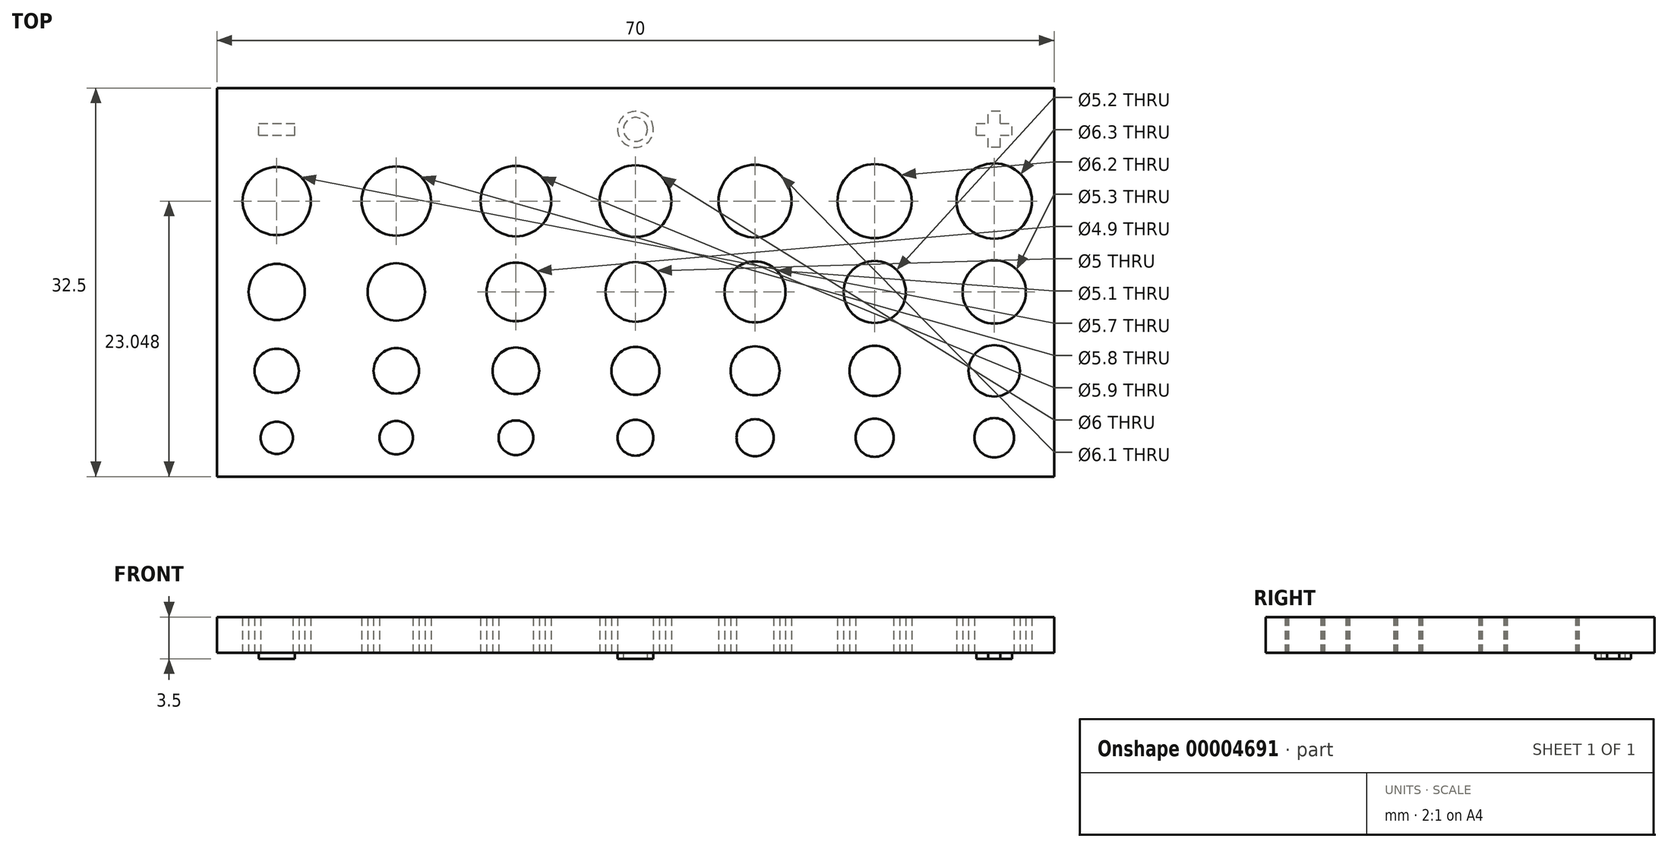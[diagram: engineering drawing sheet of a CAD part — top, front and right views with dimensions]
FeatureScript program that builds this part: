
annotation { "Feature Type Name" : "Feature", "Feature Type Description" : "" }
export const myFeature = defineFeature(function(context is Context, id is Id, definition is map)
    precondition{}
    {
        {
            var Q0;
            Q0=qCreatedBy(makeId("Top.planeOp"),FACE);
            var sketch = newSketch(context, id + "F0", { "sketchPlane" : qUnion([Q0])});
            skLineSegment(sketch, "E0.bottom", {"start": v(0, 0) * mm, "end": v(70, 0) * mm});
            skLineSegment(sketch, "E0.top", {"start": v(0, 32.5) * mm, "end": v(70, 32.5) * mm});
            skLineSegment(sketch, "E0.left", {"start": v(0, 0) * mm, "end": v(0, 32.5) * mm});
            skLineSegment(sketch, "E0.right", {"start": v(70, 0) * mm, "end": v(70, 32.5) * mm});
            skSolve(sketch);
        }
        {
            var Q0;
            Q0=makeQuery(id+"F0.imprint","IMPRINT",FACE,{"disambiguationData":[TD([[makeQuery(id+"F0.imprint","IMPRINT",EDGE,{"derivedFrom":sQuery(id+"F0.wireOp",EDGE,"E0.bottom")}),1.0]])]});
            extrude(context, id + "F1", {"entities" : qUnion([Q0]), "depth" : 3 * mm});
        }
        {
            var Q0;
            Q0=qCreatedBy(makeId("Top.planeOp"),FACE);
            var sketch = newSketch(context, id + "F2", { "sketchPlane" : qUnion([Q0])});
            skLineSegment(sketch, "E1", {"start": v(-5, 15.45) * mm, "end": v(5, 15.45) * mm, "construction": true});
            skLineSegment(sketch, "E2", {"start": v(5, 15.45) * mm, "end": v(15, 15.45) * mm, "construction": true});
            skLineSegment(sketch, "E3", {"start": v(15, 15.45) * mm, "end": v(25, 15.45) * mm, "construction": true});
            skLineSegment(sketch, "E4", {"start": v(25, 15.45) * mm, "end": v(35, 15.45) * mm, "construction": true});
            skLineSegment(sketch, "E5", {"start": v(35, 15.45) * mm, "end": v(45, 15.45) * mm, "construction": true});
            skLineSegment(sketch, "E6", {"start": v(45, 15.45) * mm, "end": v(55, 15.45) * mm, "construction": true});
            skLineSegment(sketch, "E7", {"start": v(-5, 23.05) * mm, "end": v(5, 23.05) * mm, "construction": true});
            skLineSegment(sketch, "E8", {"start": v(5, 23.05) * mm, "end": v(15, 23.05) * mm, "construction": true});
            skLineSegment(sketch, "E9", {"start": v(15, 23.05) * mm, "end": v(25, 23.05) * mm, "construction": true});
            skLineSegment(sketch, "E10", {"start": v(25, 23.05) * mm, "end": v(35, 23.05) * mm, "construction": true});
            skLineSegment(sketch, "E11", {"start": v(35, 23.05) * mm, "end": v(45, 23.05) * mm, "construction": true});
            skLineSegment(sketch, "E12", {"start": v(45, 23.05) * mm, "end": v(55, 23.05) * mm, "construction": true});
            skLineSegment(sketch, "E13", {"start": v(55, 3.25) * mm, "end": v(45, 3.25) * mm, "construction": true});
            skLineSegment(sketch, "E14", {"start": v(45, 3.25) * mm, "end": v(35, 3.25) * mm, "construction": true});
            skLineSegment(sketch, "E15", {"start": v(35, 3.25) * mm, "end": v(25, 3.25) * mm, "construction": true});
            skLineSegment(sketch, "E16", {"start": v(25, 3.25) * mm, "end": v(15, 3.25) * mm, "construction": true});
            skLineSegment(sketch, "E17", {"start": v(15, 3.25) * mm, "end": v(5, 3.25) * mm, "construction": true});
            skLineSegment(sketch, "E18", {"start": v(5, 3.25) * mm, "end": v(-5, 3.25) * mm, "construction": true});
            skCircle(sketch, "E19", {"center": v(5, 15.45) * mm, "radius": 2.35 * mm});
            skCircle(sketch, "E20", {"center": v(15, 15.45) * mm, "radius": 2.4 * mm});
            skCircle(sketch, "E21", {"center": v(25, 15.45) * mm, "radius": 2.45 * mm});
            skCircle(sketch, "E22", {"center": v(35, 15.45) * mm, "radius": 2.5 * mm});
            skCircle(sketch, "E23", {"center": v(45, 15.45) * mm, "radius": 2.55 * mm});
            skCircle(sketch, "E24", {"center": v(5, 23.05) * mm, "radius": 2.85 * mm});
            skCircle(sketch, "E25", {"center": v(15, 23.05) * mm, "radius": 2.9 * mm});
            skCircle(sketch, "E26", {"center": v(25, 23.05) * mm, "radius": 2.95 * mm});
            skCircle(sketch, "E27", {"center": v(35, 23.05) * mm, "radius": 3 * mm});
            skCircle(sketch, "E28", {"center": v(45, 23.05) * mm, "radius": 3.05 * mm});
            skCircle(sketch, "E29", {"center": v(5, 3.25) * mm, "radius": 1.35 * mm});
            skCircle(sketch, "E30", {"center": v(15, 3.25) * mm, "radius": 1.4 * mm});
            skCircle(sketch, "E31", {"center": v(25, 3.25) * mm, "radius": 1.45 * mm});
            skCircle(sketch, "E32", {"center": v(35, 3.25) * mm, "radius": 1.5 * mm});
            skCircle(sketch, "E33", {"center": v(45, 3.25) * mm, "radius": 1.55 * mm});
            skLineSegment(sketch, "E34", {"start": v(-5, 8.85) * mm, "end": v(5, 8.85) * mm, "construction": true});
            skLineSegment(sketch, "E35", {"start": v(5, 8.85) * mm, "end": v(15, 8.85) * mm, "construction": true});
            skLineSegment(sketch, "E36", {"start": v(15, 8.85) * mm, "end": v(25, 8.85) * mm, "construction": true});
            skLineSegment(sketch, "E37", {"start": v(25, 8.85) * mm, "end": v(35, 8.85) * mm, "construction": true});
            skLineSegment(sketch, "E38", {"start": v(35, 8.85) * mm, "end": v(45, 8.85) * mm, "construction": true});
            skLineSegment(sketch, "E39", {"start": v(45, 8.85) * mm, "end": v(55, 8.85) * mm, "construction": true});
            skCircle(sketch, "E40", {"center": v(5, 8.85) * mm, "radius": 1.85 * mm});
            skCircle(sketch, "E41", {"center": v(15, 8.85) * mm, "radius": 1.9 * mm});
            skCircle(sketch, "E42", {"center": v(25, 8.85) * mm, "radius": 1.95 * mm});
            skCircle(sketch, "E43", {"center": v(35, 8.85) * mm, "radius": 2 * mm});
            skCircle(sketch, "E44", {"center": v(45, 8.85) * mm, "radius": 2.05 * mm});
            skLineSegment(sketch, "E45", {"start": v(45, 3.25) * mm, "end": v(45, 8.85) * mm, "construction": true});
            skLineSegment(sketch, "E46", {"start": v(45, 8.85) * mm, "end": v(45, 15.45) * mm, "construction": true});
            skLineSegment(sketch, "E47", {"start": v(45, 23.05) * mm, "end": v(45, 15.45) * mm, "construction": true});
            skLineSegment(sketch, "E48", {"start": v(55, 3.25) * mm, "end": v(65, 3.25) * mm, "construction": true});
            skLineSegment(sketch, "E49", {"start": v(65, 3.25) * mm, "end": v(75, 3.25) * mm, "construction": true});
            skLineSegment(sketch, "E50", {"start": v(55, 8.85) * mm, "end": v(65, 8.85) * mm, "construction": true});
            skLineSegment(sketch, "E51", {"start": v(65, 8.85) * mm, "end": v(75, 8.85) * mm, "construction": true});
            skLineSegment(sketch, "E52", {"start": v(55, 15.45) * mm, "end": v(65, 15.45) * mm, "construction": true});
            skLineSegment(sketch, "E53", {"start": v(65, 15.45) * mm, "end": v(75, 15.45) * mm, "construction": true});
            skLineSegment(sketch, "E54", {"start": v(55, 23.05) * mm, "end": v(65, 23.05) * mm, "construction": true});
            skLineSegment(sketch, "E55", {"start": v(65, 23.05) * mm, "end": v(75, 23.05) * mm, "construction": true});
            skCircle(sketch, "E56", {"center": v(55, 3.25) * mm, "radius": 1.6 * mm});
            skCircle(sketch, "E57", {"center": v(65, 3.25) * mm, "radius": 1.65 * mm});
            skCircle(sketch, "E58", {"center": v(55, 8.85) * mm, "radius": 2.1 * mm});
            skCircle(sketch, "E59", {"center": v(65, 8.85) * mm, "radius": 2.15 * mm});
            skCircle(sketch, "E60", {"center": v(55, 15.45) * mm, "radius": 2.6 * mm});
            skCircle(sketch, "E61", {"center": v(65, 15.45) * mm, "radius": 2.65 * mm});
            skCircle(sketch, "E62", {"center": v(55, 23.05) * mm, "radius": 3.1 * mm});
            skCircle(sketch, "E63", {"center": v(65, 23.05) * mm, "radius": 3.15 * mm});
            skPoint(sketch, "E64", {"position": v(70, 3.25) * mm});
            skPoint(sketch, "E65", {"position": v(0, 3.25) * mm});
            skSolve(sketch);
        }
        {
            var Q0;
            Q0 = qSketchRegion(id + "F2", true);
            extrude(context, id + "F3", {"entities" : qUnion([Q0]), "operationType" : NewBodyOperationType.REMOVE, "depth" : 5 * mm});
        }
        {
            var Q0;
            Q0=qCreatedBy(makeId("Top.planeOp"),FACE);
            var sketch = newSketch(context, id + "F4", { "sketchPlane" : qUnion([Q0])});
            skLineSegment(sketch, "E66", {"start": v(5, 29.05) * mm, "end": v(20, 29.05) * mm, "construction": true});
            skLineSegment(sketch, "E67", {"start": v(20, 29.05) * mm, "end": v(35, 29.05) * mm, "construction": true});
            skLineSegment(sketch, "E68", {"start": v(35, 29.05) * mm, "end": v(50, 29.05) * mm, "construction": true});
            skLineSegment(sketch, "E69", {"start": v(50, 29.05) * mm, "end": v(65, 29.05) * mm, "construction": true});
            skLineSegment(sketch, "E70.bottom", {"start": v(3.5, 28.55) * mm, "end": v(6.5, 28.55) * mm});
            skLineSegment(sketch, "E70.top", {"start": v(3.5, 29.55) * mm, "end": v(6.5, 29.55) * mm});
            skLineSegment(sketch, "E70.left", {"start": v(3.5, 28.55) * mm, "end": v(3.5, 29.55) * mm});
            skLineSegment(sketch, "E70.right", {"start": v(6.5, 28.55) * mm, "end": v(6.5, 29.55) * mm});
            skLineSegment(sketch, "E71", {"start": v(3.5, 29.55) * mm, "end": v(6.5, 28.55) * mm, "construction": true});
            skCircle(sketch, "E72", {"center": v(35, 29.05) * mm, "radius": 1.5 * mm});
            skCircle(sketch, "E73", {"center": v(35, 29.05) * mm, "radius": 1 * mm});
            skLineSegment(sketch, "E74", {"start": v(5, 29.05) * mm, "end": v(5, 23.05) * mm, "construction": true});
            skLineSegment(sketch, "E75", {"start": v(65, 29.05) * mm, "end": v(65, 23.05) * mm, "construction": true});
            skLineSegment(sketch, "E76.bottom", {"start": v(63.5, 28.55) * mm, "end": v(64.5, 28.55) * mm});
            skLineSegment(sketch, "E76.top", {"start": v(63.5, 29.55) * mm, "end": v(64.5, 29.55) * mm});
            skLineSegment(sketch, "E76.left", {"start": v(63.5, 28.55) * mm, "end": v(63.5, 29.55) * mm});
            skLineSegment(sketch, "E76.right", {"start": v(66.5, 28.55) * mm, "end": v(66.5, 29.55) * mm});
            skLineSegment(sketch, "E77.bottom", {"start": v(65.5, 27.55) * mm, "end": v(64.5, 27.55) * mm});
            skLineSegment(sketch, "E77.top", {"start": v(65.5, 30.55) * mm, "end": v(64.5, 30.55) * mm});
            skLineSegment(sketch, "E77.left", {"start": v(65.5, 27.55) * mm, "end": v(65.5, 28.55) * mm});
            skLineSegment(sketch, "E77.right", {"start": v(64.5, 27.55) * mm, "end": v(64.5, 28.55) * mm});
            skLineSegment(sketch, "E78.trimOffspring", {"start": v(64.5, 29.55) * mm, "end": v(64.5, 30.55) * mm});
            skLineSegment(sketch, "E79.trimOffspring", {"start": v(65.5, 28.55) * mm, "end": v(66.5, 28.55) * mm});
            skLineSegment(sketch, "E80.trimOffspring", {"start": v(65.5, 29.55) * mm, "end": v(65.5, 30.55) * mm});
            skLineSegment(sketch, "E81.trimOffspring", {"start": v(65.5, 29.55) * mm, "end": v(66.5, 29.55) * mm});
            skLineSegment(sketch, "E82", {"start": v(64.5, 29.55) * mm, "end": v(65.5, 28.55) * mm, "construction": true});
            skPoint(sketch, "E83", {"position": v(65, 29.05) * mm});
            skSolve(sketch);
        }
        {
            var Q0;
            Q0 = qSketchRegion(id + "F4", true);
            extrude(context, id + "F5", {"entities" : qUnion([Q0]), "operationType" : NewBodyOperationType.ADD, "oppositeDirection" : true, "depth" : 0.5 * mm});
        }
    });
